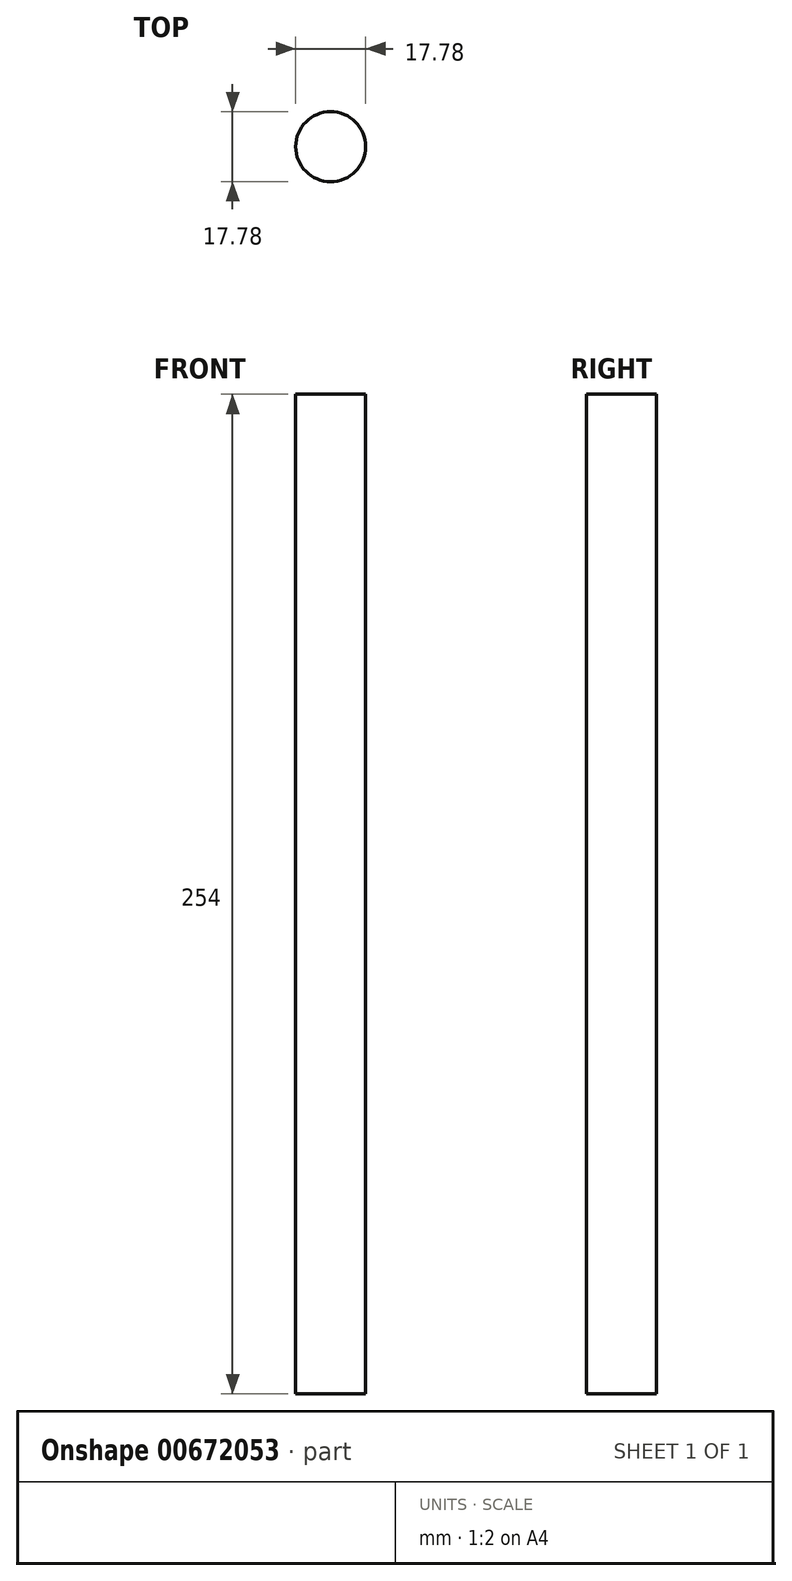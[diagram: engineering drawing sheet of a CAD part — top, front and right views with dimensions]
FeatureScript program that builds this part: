
annotation { "Feature Type Name" : "Feature", "Feature Type Description" : "" }
export const myFeature = defineFeature(function(context is Context, id is Id, definition is map)
    precondition{}
    {
        {
            var Q0;
            Q0=qCreatedBy(makeId("Top.planeOp"),FACE);
            var sketch = newSketch(context, id + "F0", { "sketchPlane" : qUnion([Q0])});
            skCircle(sketch, "E0", {"center": v(0, 0) * mm, "radius": 8.9 * mm});
            skSolve(sketch);
        }
        {
            var Q0;
            Q0=makeQuery(id+"F0.imprint","IMPRINT",FACE,{"disambiguationData":[TD([[makeQuery(id+"F0.imprint","IMPRINT",EDGE,{"derivedFrom":sQuery(id+"F0.wireOp",EDGE,"E0")}),1.0]])]});
            extrude(context, id + "F1", {"entities" : qUnion([Q0]), "oppositeDirection" : true, "depth" : 254 * mm, "offsetDistance" : 25.4 * mm});
        }
    });
